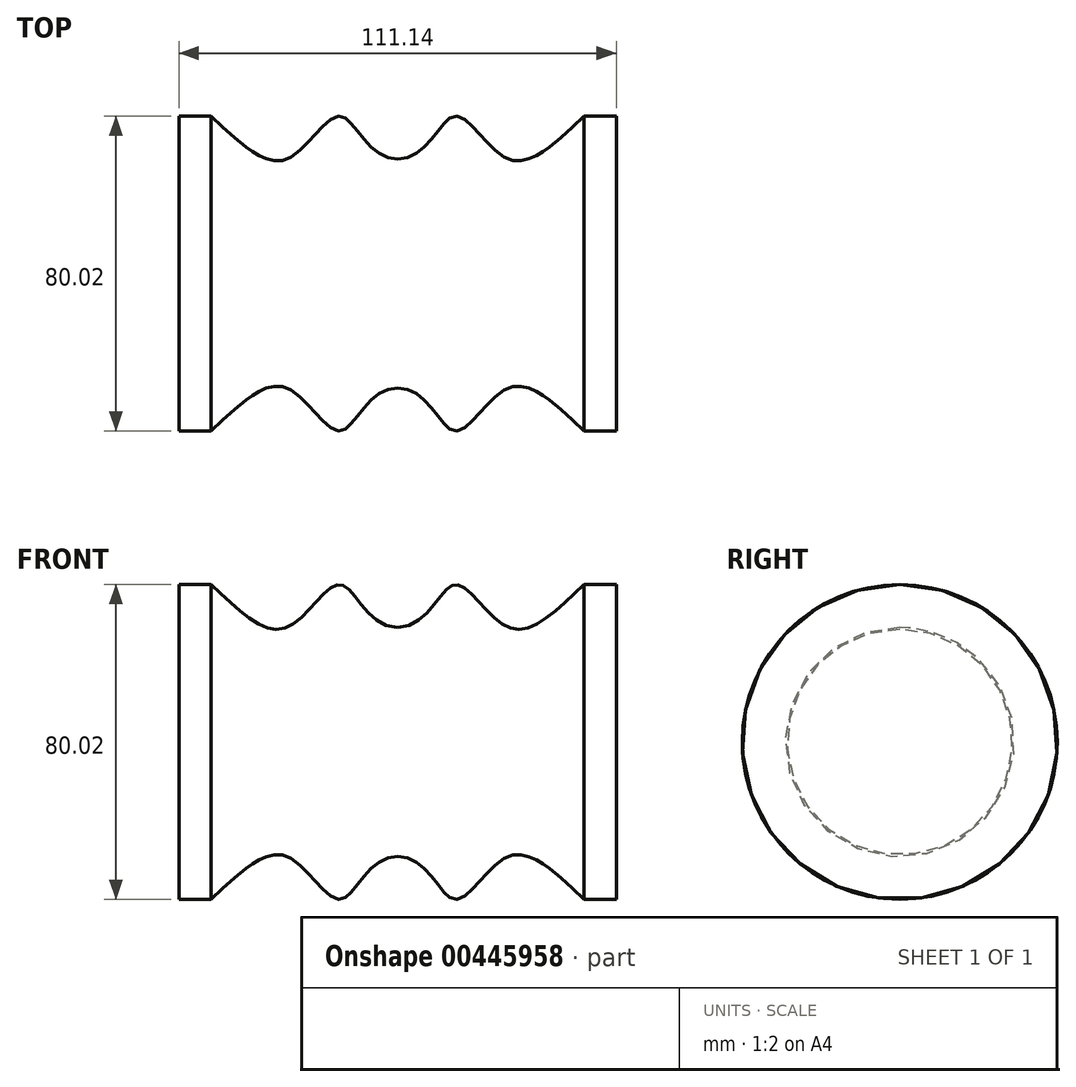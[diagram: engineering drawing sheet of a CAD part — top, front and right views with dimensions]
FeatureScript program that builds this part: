
annotation { "Feature Type Name" : "Feature", "Feature Type Description" : "" }
export const myFeature = defineFeature(function(context is Context, id is Id, definition is map)
    precondition{}
    {
        {
            var Q0;
            Q0=qCreatedBy(makeId("Top.planeOp"),FACE);
            var sketch = newSketch(context, id + "F0", { "sketchPlane" : qUnion([Q0])});
            skLineSegment(sketch, "E0", {"start": v(55.57, 0) * mm, "end": v(55.57, -40) * mm});
            skLineSegment(sketch, "E1", {"start": v(55.57, -40) * mm, "end": v(47.4, -40) * mm});
            skLineSegment(sketch, "E2", {"start": v(0, 66.91) * mm, "end": v(0, -54.64) * mm, "construction": true});
            skLineSegment(sketch, "E3", {"start": v(86.43, -29.08) * mm, "end": v(-109.85, -29.08) * mm, "construction": true});
            skLineSegment(sketch, "E4", {"start": v(78.11, -40) * mm, "end": v(-44.85, -40) * mm, "construction": true});
            skFitSpline(sketch, "E5", {"points": [v(47.4, -40) * mm, v(28.15, -29.08) * mm, v(14.56, -40) * mm, v(0, -29.08) * mm], "startDerivative": vector(-57.02, 53.48) * mm, "endDerivative": vector(-72.52, 0) * mm});
            skLineSegment(sketch, "E6", {"start": v(55.57, 0) * mm, "end": v(0, 0) * mm});
            skLineSegment(sketch, "E7.MirrorCS", {"start": v(-55.57, 0) * mm, "end": v(0, 0) * mm});
            skLineSegment(sketch, "E8.MirrorCS", {"start": v(-55.57, 0) * mm, "end": v(-55.57, -40) * mm});
            skLineSegment(sketch, "E9.MirrorCS", {"start": v(-55.57, -40) * mm, "end": v(-47.4, -40) * mm});
            skFitSpline(sketch, "E10.MirrorCS", {"points": [v(-47.4, -40) * mm, v(-28.15, -29.08) * mm, v(-14.56, -40) * mm, v(0, -29.08) * mm], "startDerivative": vector(57.02, 53.48) * mm, "endDerivative": vector(72.52, 0) * mm});
            skSolve(sketch);
        }
        {
            var Q0;
            Q0=makeQuery(id+"F0.imprint","IMPRINT",FACE,{"disambiguationData":[TD([[makeQuery(id+"F0.imprint","IMPRINT",EDGE,{"derivedFrom":sQuery(id+"F0.wireOp",EDGE,"E0")}),-1.0]])]});
            var Q1;
            Q1=sQuery(id+"F0.wireOp",EDGE,"E7.MirrorCS");
            revolve(context, id + "F1", {"surfaceOperationType" : NewSurfaceOperationType.NEW, "entities" : qUnion([Q0]), "axis" : qUnion([Q1]), "revolveType" : RevolveType.FULL});
        }
    });
